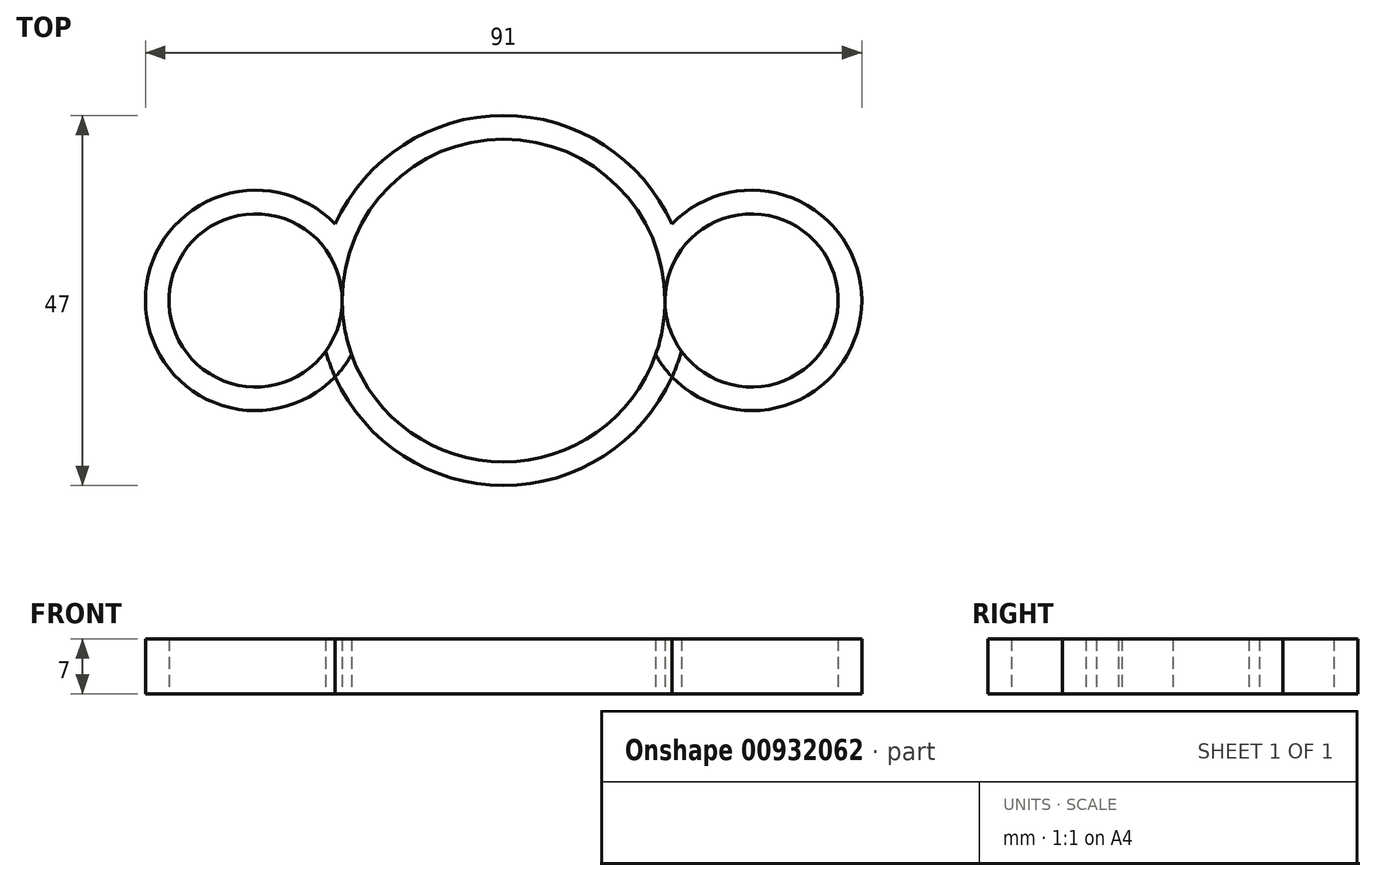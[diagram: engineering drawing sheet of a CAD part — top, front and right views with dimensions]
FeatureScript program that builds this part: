
annotation { "Feature Type Name" : "Feature", "Feature Type Description" : "" }
export const myFeature = defineFeature(function(context is Context, id is Id, definition is map)
    precondition{}
    {
        {
            var Q0;
            Q0=qCreatedBy(makeId("Top.planeOp"),FACE);
            var sketch = newSketch(context, id + "F0", { "sketchPlane" : qUnion([Q0])});
            skCircle(sketch, "E0", {"center": v(0, 0) * mm, "radius": 20.5 * mm});
            skCircle(sketch, "E1", {"center": v(-31.5, 0) * mm, "radius": 11 * mm});
            skCircle(sketch, "E2", {"center": v(31.5, 0) * mm, "radius": 11 * mm});
            skCircle(sketch, "E3.0", {"center": v(-31.5, 0) * mm, "radius": 14 * mm});
            skCircle(sketch, "E4.0", {"center": v(0, 0) * mm, "radius": 23.5 * mm});
            skCircle(sketch, "E5.0", {"center": v(31.5, 0) * mm, "radius": 14 * mm});
            skSolve(sketch);
        }
        {
            var Q0;
            {var subQ0=sQuery(id+"F0.wireOp",EDGE,"E4.0");var subQ1=sQuery(id+"F0.wireOp",EDGE,"E1");var subQ2=makeQuery(id+"F0.imprint","INTERSECT",VERTEX,{"disambiguationData":[OD(0.0)],"derivedFrom":[subQ1,subQ0]});Q0=makeQuery(id+"F0.imprint","IMPRINT",FACE,{"disambiguationData":[TD([[makeQuery(id+"F0.imprint","IMPRINT",EDGE,{"disambiguationData":[TD([[subQ2,-1.0]])],"derivedFrom":subQ1}),-1.0]])]});}
            var Q1;
            {var subQ0=sQuery(id+"F0.wireOp",EDGE,"E3.0");var subQ1=sQuery(id+"F0.wireOp",EDGE,"E0");var subQ2=makeQuery(id+"F0.imprint","INTERSECT",VERTEX,{"disambiguationData":[OD(1.0)],"derivedFrom":[subQ1,subQ0]});Q1=makeQuery(id+"F0.imprint","IMPRINT",FACE,{"disambiguationData":[TD([[makeQuery(id+"F0.imprint","IMPRINT",EDGE,{"disambiguationData":[TD([[subQ2,-1.0]])],"derivedFrom":subQ1}),-1.0]])]});}
            var Q2;
            {var subQ0=sQuery(id+"F0.wireOp",EDGE,"E5.0");var subQ1=sQuery(id+"F0.wireOp",EDGE,"E0");var subQ2=makeQuery(id+"F0.imprint","INTERSECT",VERTEX,{"disambiguationData":[OD(0.0)],"derivedFrom":[subQ1,subQ0]});Q2=makeQuery(id+"F0.imprint","IMPRINT",FACE,{"disambiguationData":[TD([[makeQuery(id+"F0.imprint","IMPRINT",EDGE,{"disambiguationData":[TD([[subQ2,-1.0]])],"derivedFrom":subQ1}),-1.0]])]});}
            var Q3;
            {var subQ0=sQuery(id+"F0.wireOp",EDGE,"E4.0");var subQ1=sQuery(id+"F0.wireOp",EDGE,"E2");var subQ2=makeQuery(id+"F0.imprint","INTERSECT",VERTEX,{"disambiguationData":[OD(0.0)],"derivedFrom":[subQ1,subQ0]});Q3=makeQuery(id+"F0.imprint","IMPRINT",FACE,{"disambiguationData":[TD([[makeQuery(id+"F0.imprint","IMPRINT",EDGE,{"disambiguationData":[TD([[subQ2,1.0]])],"derivedFrom":subQ1}),-1.0]])]});}
            var Q4;
            {var subQ0=sQuery(id+"F0.wireOp",EDGE,"E3.0");var subQ1=sQuery(id+"F0.wireOp",EDGE,"E0");var subQ2=makeQuery(id+"F0.imprint","INTERSECT",VERTEX,{"disambiguationData":[OD(0.0)],"derivedFrom":[subQ1,subQ0]});Q4=makeQuery(id+"F0.imprint","IMPRINT",FACE,{"disambiguationData":[TD([[makeQuery(id+"F0.imprint","IMPRINT",EDGE,{"disambiguationData":[TD([[subQ2,-1.0]])],"derivedFrom":subQ1}),-1.0]])]});}
            var Q5;
            {var subQ0=sQuery(id+"F0.wireOp",EDGE,"E5.0");var subQ1=sQuery(id+"F0.wireOp",EDGE,"E0");var subQ2=makeQuery(id+"F0.imprint","INTERSECT",VERTEX,{"disambiguationData":[OD(0.0)],"derivedFrom":[subQ1,subQ0]});Q5=makeQuery(id+"F0.imprint","IMPRINT",FACE,{"disambiguationData":[TD([[makeQuery(id+"F0.imprint","IMPRINT",EDGE,{"disambiguationData":[TD([[subQ2,1.0]])],"derivedFrom":subQ1}),-1.0]])]});}
            extrude(context, id + "F1", {"entities" : qUnion([Q0, Q1, Q2, Q3, Q4, Q5]), "depth" : 7 * mm, "offsetDistance" : 25 * mm});
        }
        {
            var Q0;
            Q0=qCreatedBy(makeId("Top.planeOp"),FACE);
            var sketch = newSketch(context, id + "F2", { "sketchPlane" : qUnion([Q0])});
            skCircle(sketch, "E6", {"center": v(0, 0) * mm, "radius": 20.5 * mm});
            skCircle(sketch, "E7", {"center": v(-31.5, 0) * mm, "radius": 11 * mm});
            skCircle(sketch, "E8", {"center": v(31.5, 0) * mm, "radius": 11 * mm});
            skCircle(sketch, "E9.0", {"center": v(-31.5, 0) * mm, "radius": 14 * mm});
            skCircle(sketch, "E10.0", {"center": v(0, 0) * mm, "radius": 23.5 * mm});
            skCircle(sketch, "E11.0", {"center": v(31.5, 0) * mm, "radius": 14 * mm});
            skSolve(sketch);
        }
        {
            var Q0;
            {var subQ0=sQuery(id+"F2.wireOp",EDGE,"E7");var subQ1=sQuery(id+"F2.wireOp",EDGE,"E6");var subQ2=makeQuery(id+"F2.imprint","INTERSECT",VERTEX,{"derivedFrom":[subQ1,subQ0]});Q0=makeQuery(id+"F2.imprint","IMPRINT",FACE,{"disambiguationData":[TD([[makeQuery(id+"F2.imprint","IMPRINT",EDGE,{"disambiguationData":[TD([[subQ2,-1.0]])],"derivedFrom":subQ1}),-1.0]])]});}
            var Q1;
            {var subQ0=sQuery(id+"F2.wireOp",EDGE,"E8");var subQ1=sQuery(id+"F2.wireOp",EDGE,"E6");var subQ2=makeQuery(id+"F2.imprint","INTERSECT",VERTEX,{"derivedFrom":[subQ1,subQ0]});Q1=makeQuery(id+"F2.imprint","IMPRINT",FACE,{"disambiguationData":[TD([[makeQuery(id+"F2.imprint","IMPRINT",EDGE,{"disambiguationData":[TD([[subQ2,1.0]])],"derivedFrom":subQ1}),-1.0]])]});}
            extrude(context, id + "F3", {"entities" : qUnion([Q0, Q1]), "depth" : 7 * mm, "offsetDistance" : 25 * mm});
        }
    });
